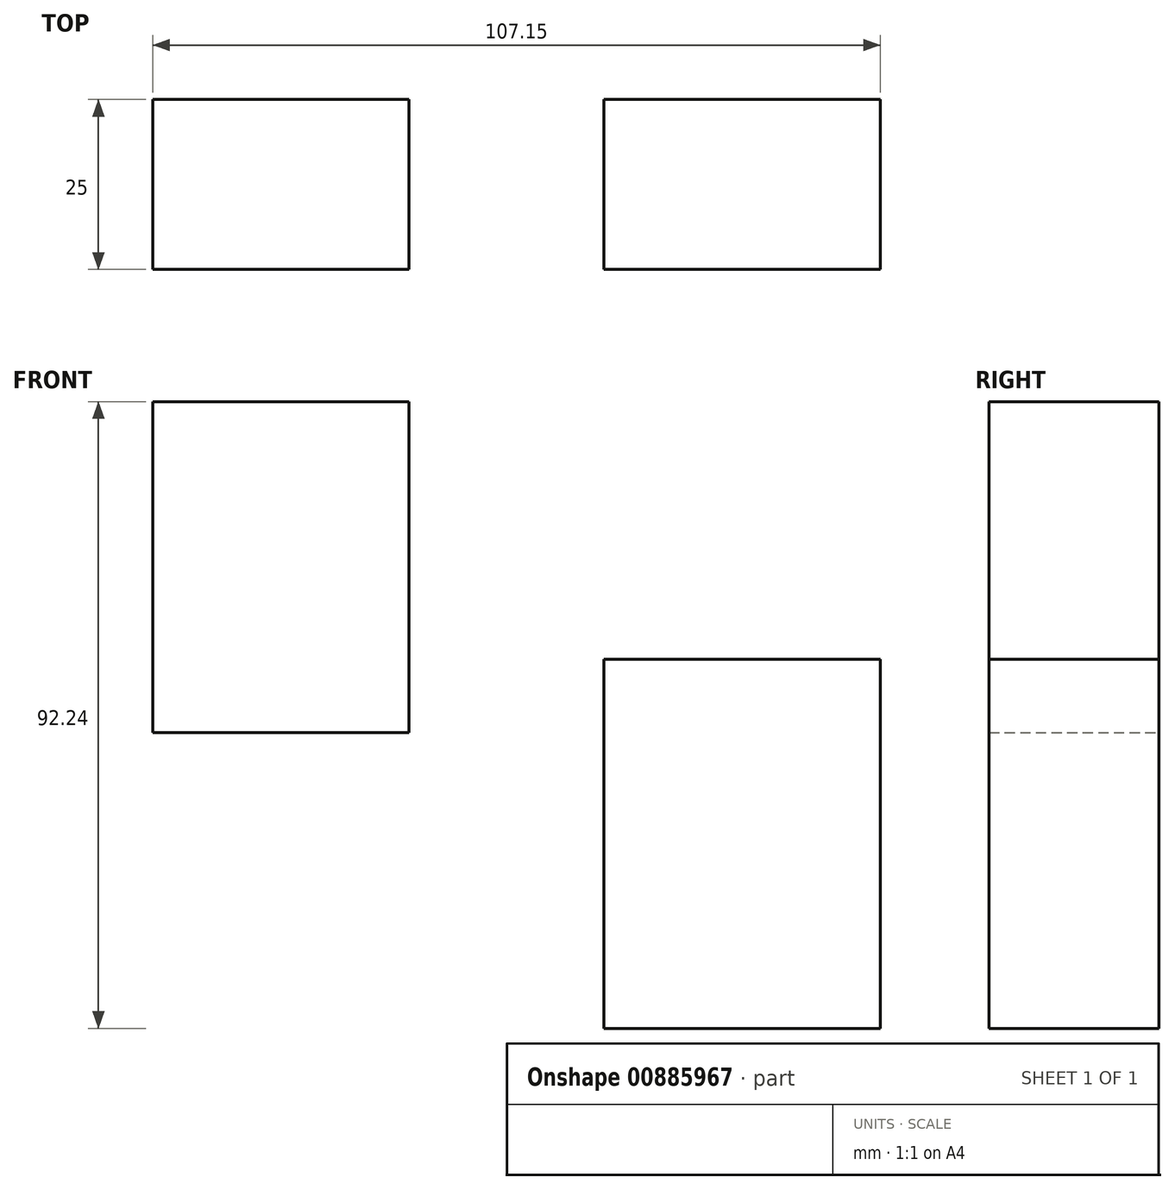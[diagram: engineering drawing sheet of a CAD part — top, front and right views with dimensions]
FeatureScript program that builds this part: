
annotation { "Feature Type Name" : "Feature", "Feature Type Description" : "" }
export const myFeature = defineFeature(function(context is Context, id is Id, definition is map)
    precondition{}
    {
        {
            var Q0;
            Q0=qCreatedBy(makeId("Front.planeOp"),FACE);
            var sketch = newSketch(context, id + "F0", { "sketchPlane" : qUnion([Q0])});
            skLineSegment(sketch, "E0.bottom", {"start": v(-122, 48.73) * mm, "end": v(-84.28, 48.73) * mm});
            skLineSegment(sketch, "E0.top", {"start": v(-122, 0) * mm, "end": v(-84.28, 0) * mm});
            skLineSegment(sketch, "E0.left", {"start": v(-122, 48.73) * mm, "end": v(-122, 0) * mm});
            skLineSegment(sketch, "E0.right", {"start": v(-84.28, 48.73) * mm, "end": v(-84.28, 0) * mm});
            skLineSegment(sketch, "E1.bottom", {"start": v(-55.58, 10.83) * mm, "end": v(-14.85, 10.83) * mm});
            skLineSegment(sketch, "E1.top", {"start": v(-55.58, -43.5) * mm, "end": v(-14.85, -43.5) * mm});
            skLineSegment(sketch, "E1.left", {"start": v(-55.58, 10.83) * mm, "end": v(-55.58, -43.5) * mm});
            skLineSegment(sketch, "E1.right", {"start": v(-14.85, 10.83) * mm, "end": v(-14.85, -43.5) * mm});
            skSolve(sketch);
        }
        {
            var Q0;
            Q0 = qSketchRegion(id + "F0", true);
            extrude(context, id + "F1", {"entities" : qUnion([Q0]), "depth" : 25 * mm, "offsetDistance" : 25 * mm});
        }
    });
